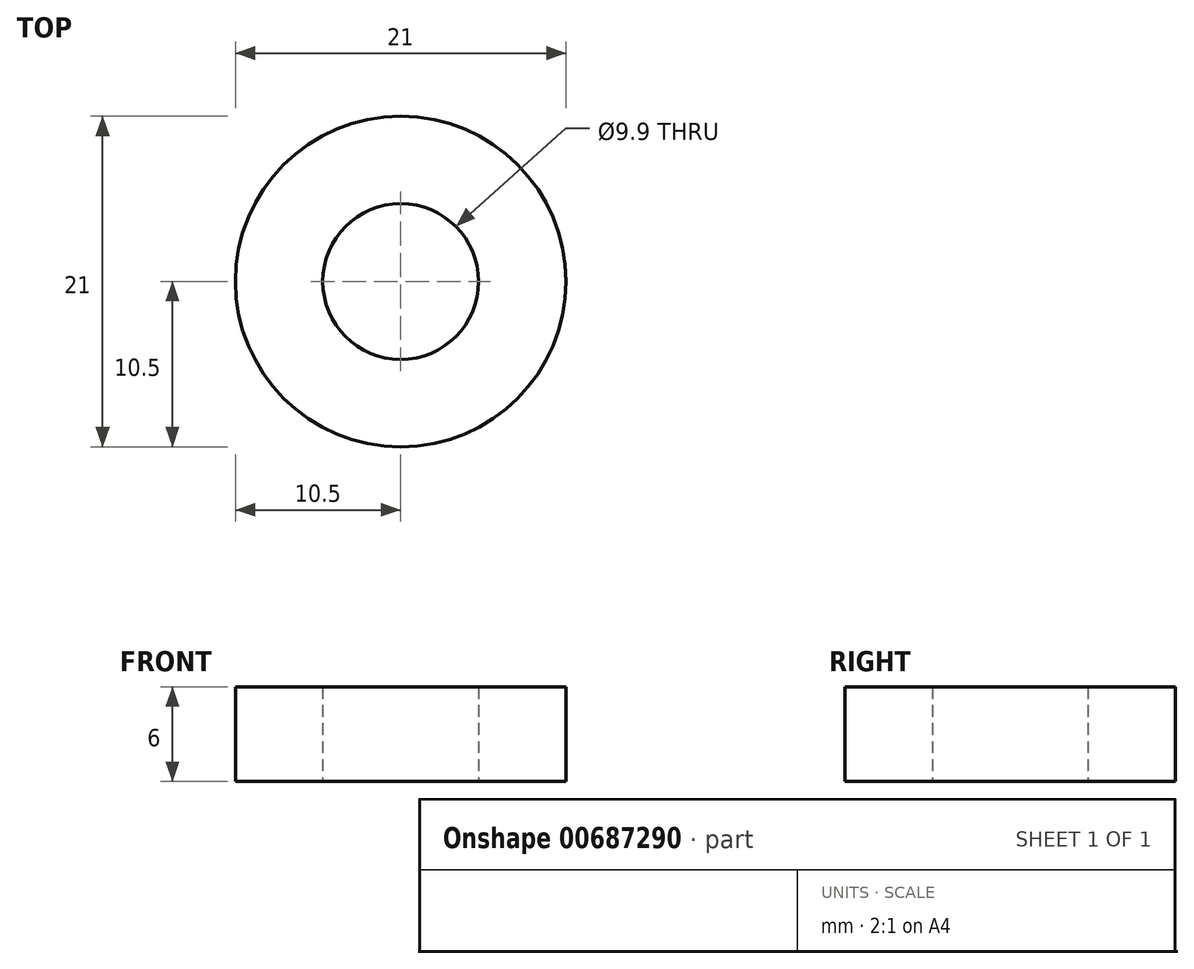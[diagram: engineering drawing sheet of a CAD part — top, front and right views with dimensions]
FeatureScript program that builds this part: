
annotation { "Feature Type Name" : "Feature", "Feature Type Description" : "" }
export const myFeature = defineFeature(function(context is Context, id is Id, definition is map)
    precondition{}
    {
        {
            var Q0;
            Q0=qCreatedBy(makeId("Top.planeOp"),FACE);
            var sketch = newSketch(context, id + "F0", { "sketchPlane" : qUnion([Q0])});
            skCircle(sketch, "E0", {"center": v(0, 0) * mm, "radius": 10.5 * mm});
            skCircle(sketch, "E1", {"center": v(0, 0) * mm, "radius": 4.95 * mm});
            skSolve(sketch);
        }
        {
            var Q0;
            Q0=makeQuery(id+"F0.imprint","IMPRINT",FACE,{"disambiguationData":[TD([[makeQuery(id+"F0.imprint","IMPRINT",EDGE,{"derivedFrom":sQuery(id+"F0.wireOp",EDGE,"E0")}),1.0]])]});
            extrude(context, id + "F1", {"entities" : qUnion([Q0]), "depth" : 6 * mm, "offsetDistance" : 25 * mm});
        }
    });
